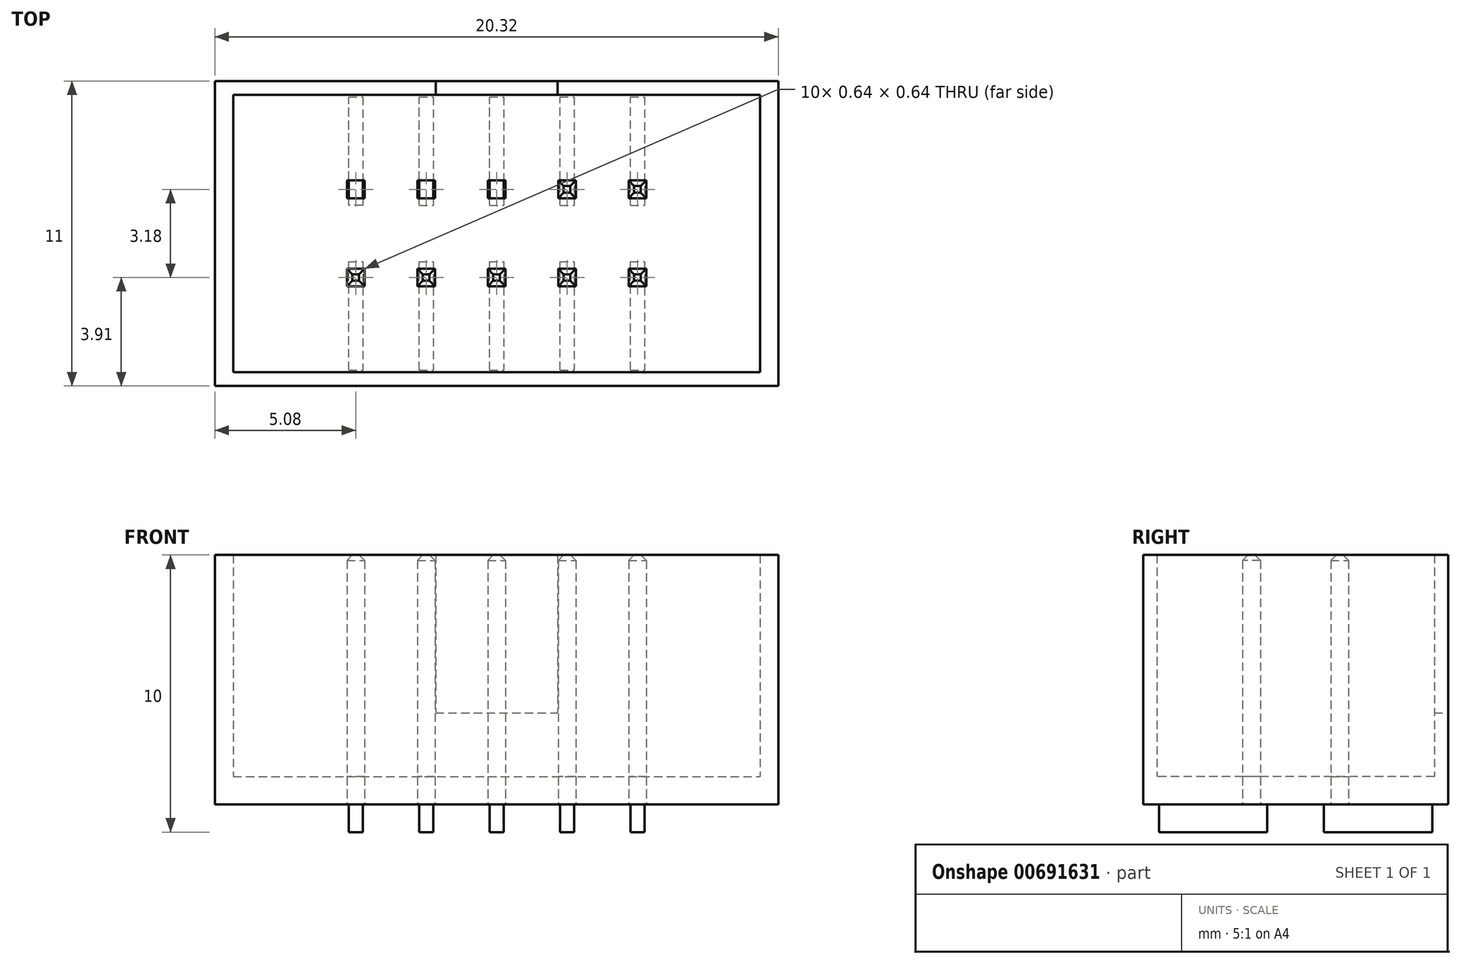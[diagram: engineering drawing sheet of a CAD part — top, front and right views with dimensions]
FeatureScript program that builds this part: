
annotation { "Feature Type Name" : "Feature", "Feature Type Description" : "" }
export const myFeature = defineFeature(function(context is Context, id is Id, definition is map)
    precondition{}
    {
        {
            var Q0;
            Q0=qCreatedBy(makeId("Top.planeOp"),FACE);
            var sketch = newSketch(context, id + "F0", { "sketchPlane" : qUnion([Q0])});
            skLineSegment(sketch, "E0.bottom", {"start": v(10.16, 5.5) * mm, "end": v(-10.16, 5.5) * mm});
            skLineSegment(sketch, "E0.top", {"start": v(10.16, -5.5) * mm, "end": v(-10.16, -5.5) * mm});
            skLineSegment(sketch, "E0.left", {"start": v(10.16, 5.5) * mm, "end": v(10.16, -5.5) * mm});
            skLineSegment(sketch, "E0.right", {"start": v(-10.16, 5.5) * mm, "end": v(-10.16, -5.5) * mm});
            skPoint(sketch, "E0.middle", {"position": v(0, 0) * mm});
            skLineSegment(sketch, "E1.bottom", {"start": v(-9.5, 5) * mm, "end": v(9.5, 5) * mm});
            skLineSegment(sketch, "E1.top", {"start": v(-9.5, -5) * mm, "end": v(9.5, -5) * mm});
            skLineSegment(sketch, "E1.left", {"start": v(-9.5, 5) * mm, "end": v(-9.5, -5) * mm});
            skLineSegment(sketch, "E1.right", {"start": v(9.5, 5) * mm, "end": v(9.5, -5) * mm});
            skLineSegment(sketch, "E2", {"start": v(-0.32, 1.27) * mm, "end": v(0.32, 1.27) * mm});
            skLineSegment(sketch, "E3", {"start": v(-0.32, 1.27) * mm, "end": v(-0.32, 1.9) * mm});
            skLineSegment(sketch, "E4", {"start": v(-0.32, 1.9) * mm, "end": v(0.32, 1.9) * mm});
            skLineSegment(sketch, "E5", {"start": v(0.32, 1.9) * mm, "end": v(0.32, 1.27) * mm});
            skLineSegment(sketch, "E6.MirrorCS", {"start": v(0.32, 1.27) * mm, "end": v(-0.32, 1.27) * mm});
            skLineSegment(sketch, "E7.MirrorCS", {"start": v(-0.32, 1.9) * mm, "end": v(-0.32, 1.27) * mm});
            skLineSegment(sketch, "E8.MirrorCS", {"start": v(0.32, 1.9) * mm, "end": v(-0.32, 1.9) * mm});
            skLineSegment(sketch, "E9.MirrorCS", {"start": v(0.32, 1.27) * mm, "end": v(0.32, 1.9) * mm});
            skLineSegment(sketch, "E10.MirrorCS", {"start": v(0.32, -1.27) * mm, "end": v(-0.32, -1.27) * mm});
            skLineSegment(sketch, "E11.MirrorCS", {"start": v(-0.32, -1.27) * mm, "end": v(-0.32, -1.9) * mm});
            skLineSegment(sketch, "E12.MirrorCS", {"start": v(0.32, -1.9) * mm, "end": v(-0.32, -1.9) * mm});
            skLineSegment(sketch, "E13.MirrorCS", {"start": v(0.32, -1.27) * mm, "end": v(0.32, -1.9) * mm});
            skLineSegment(sketch, "E14.1.0.0", {"start": v(2.22, 1.9) * mm, "end": v(2.86, 1.9) * mm});
            skLineSegment(sketch, "E14.1.0.1", {"start": v(2.22, 1.27) * mm, "end": v(2.22, 1.91) * mm});
            skLineSegment(sketch, "E14.1.0.2", {"start": v(2.22, 1.27) * mm, "end": v(2.86, 1.27) * mm});
            skLineSegment(sketch, "E14.1.0.3", {"start": v(2.86, 1.27) * mm, "end": v(2.86, 1.91) * mm});
            skLineSegment(sketch, "E14.1.0.4", {"start": v(2.22, -1.27) * mm, "end": v(2.22, -1.9) * mm});
            skLineSegment(sketch, "E14.1.0.5", {"start": v(2.86, -1.27) * mm, "end": v(2.22, -1.27) * mm});
            skLineSegment(sketch, "E14.1.0.6", {"start": v(2.86, -1.27) * mm, "end": v(2.86, -1.9) * mm});
            skLineSegment(sketch, "E14.1.0.7", {"start": v(2.86, -1.9) * mm, "end": v(2.22, -1.9) * mm});
            skLineSegment(sketch, "E14.2.0.0", {"start": v(4.76, 1.9) * mm, "end": v(5.4, 1.9) * mm});
            skLineSegment(sketch, "E14.2.0.1", {"start": v(4.76, 1.27) * mm, "end": v(4.76, 1.91) * mm});
            skLineSegment(sketch, "E14.2.0.2", {"start": v(4.76, 1.27) * mm, "end": v(5.4, 1.27) * mm});
            skLineSegment(sketch, "E14.2.0.3", {"start": v(5.4, 1.27) * mm, "end": v(5.4, 1.91) * mm});
            skLineSegment(sketch, "E14.2.0.4", {"start": v(4.76, -1.27) * mm, "end": v(4.76, -1.9) * mm});
            skLineSegment(sketch, "E14.2.0.5", {"start": v(5.4, -1.27) * mm, "end": v(4.76, -1.27) * mm});
            skLineSegment(sketch, "E14.2.0.6", {"start": v(5.4, -1.27) * mm, "end": v(5.4, -1.9) * mm});
            skLineSegment(sketch, "E14.2.0.7", {"start": v(5.4, -1.9) * mm, "end": v(4.76, -1.9) * mm});
            skLineSegment(sketch, "E14.direction1", {"start": v(-0.32, -1.9) * mm, "end": v(2.22, -1.9) * mm, "construction": true});
            skLineSegment(sketch, "E15.1.0.0", {"start": v(-2.22, -1.27) * mm, "end": v(-2.86, -1.27) * mm});
            skLineSegment(sketch, "E15.1.0.1", {"start": v(-2.22, -1.9) * mm, "end": v(-2.86, -1.9) * mm});
            skLineSegment(sketch, "E15.1.0.2", {"start": v(-2.22, 1.27) * mm, "end": v(-2.22, 1.9) * mm});
            skLineSegment(sketch, "E15.1.0.3", {"start": v(-2.86, -1.27) * mm, "end": v(-2.86, -1.9) * mm});
            skLineSegment(sketch, "E15.1.0.4", {"start": v(-2.86, 1.27) * mm, "end": v(-2.86, 1.9) * mm});
            skPoint(sketch, "E15.1.0.5", {"position": v(-2.54, 0) * mm});
            skLineSegment(sketch, "E15.1.0.6", {"start": v(-2.86, 1.27) * mm, "end": v(-2.22, 1.27) * mm});
            skLineSegment(sketch, "E15.1.0.7", {"start": v(-2.22, -1.27) * mm, "end": v(-2.22, -1.9) * mm});
            skLineSegment(sketch, "E15.1.0.8", {"start": v(-2.22, 1.9) * mm, "end": v(-2.86, 1.9) * mm});
            skPoint(sketch, "E15.1.0.9", {"position": v(-2.54, 0) * mm});
            skLineSegment(sketch, "E15.1.0.10", {"start": v(-2.86, 1.9) * mm, "end": v(-2.22, 1.9) * mm});
            skLineSegment(sketch, "E15.1.0.11", {"start": v(-2.22, 1.27) * mm, "end": v(-2.86, 1.27) * mm});
            skLineSegment(sketch, "E15.1.0.12", {"start": v(-2.86, 1.27) * mm, "end": v(-2.86, 1.9) * mm});
            skLineSegment(sketch, "E15.1.0.13", {"start": v(-2.22, 1.9) * mm, "end": v(-2.22, 1.27) * mm});
            skLineSegment(sketch, "E15.1.0.14", {"start": v(-2.86, 1.27) * mm, "end": v(-2.22, 1.27) * mm});
            skLineSegment(sketch, "E15.1.0.15", {"start": v(-2.22, 1.9) * mm, "end": v(-2.86, 1.9) * mm});
            skLineSegment(sketch, "E15.1.0.16", {"start": v(-2.86, 1.9) * mm, "end": v(-2.86, 1.27) * mm});
            skLineSegment(sketch, "E15.1.0.17", {"start": v(-2.22, 1.27) * mm, "end": v(-2.22, 1.9) * mm});
            skLineSegment(sketch, "E15.1.0.18", {"start": v(-2.22, 1.27) * mm, "end": v(-2.86, 1.27) * mm});
            skLineSegment(sketch, "E15.2.0.0", {"start": v(-4.76, -1.27) * mm, "end": v(-5.4, -1.27) * mm});
            skLineSegment(sketch, "E15.2.0.1", {"start": v(-4.76, -1.9) * mm, "end": v(-5.4, -1.9) * mm});
            skLineSegment(sketch, "E15.2.0.2", {"start": v(-4.76, 1.27) * mm, "end": v(-4.76, 1.9) * mm});
            skLineSegment(sketch, "E15.2.0.3", {"start": v(-5.4, -1.27) * mm, "end": v(-5.4, -1.9) * mm});
            skLineSegment(sketch, "E15.2.0.4", {"start": v(-5.4, 1.27) * mm, "end": v(-5.4, 1.9) * mm});
            skPoint(sketch, "E15.2.0.5", {"position": v(-5.08, 0) * mm});
            skLineSegment(sketch, "E15.2.0.6", {"start": v(-5.4, 1.27) * mm, "end": v(-4.76, 1.27) * mm});
            skLineSegment(sketch, "E15.2.0.7", {"start": v(-4.76, -1.27) * mm, "end": v(-4.76, -1.9) * mm});
            skLineSegment(sketch, "E15.2.0.8", {"start": v(-4.76, 1.9) * mm, "end": v(-5.4, 1.9) * mm});
            skPoint(sketch, "E15.2.0.9", {"position": v(-5.08, 0) * mm});
            skLineSegment(sketch, "E15.2.0.10", {"start": v(-5.4, 1.9) * mm, "end": v(-4.76, 1.9) * mm});
            skLineSegment(sketch, "E15.2.0.11", {"start": v(-4.76, 1.27) * mm, "end": v(-5.4, 1.27) * mm});
            skLineSegment(sketch, "E15.2.0.12", {"start": v(-5.4, 1.27) * mm, "end": v(-5.4, 1.9) * mm});
            skLineSegment(sketch, "E15.2.0.13", {"start": v(-4.76, 1.9) * mm, "end": v(-4.76, 1.27) * mm});
            skLineSegment(sketch, "E15.2.0.14", {"start": v(-5.4, 1.27) * mm, "end": v(-4.76, 1.27) * mm});
            skLineSegment(sketch, "E15.2.0.15", {"start": v(-4.76, 1.9) * mm, "end": v(-5.4, 1.9) * mm});
            skLineSegment(sketch, "E15.2.0.16", {"start": v(-5.4, 1.9) * mm, "end": v(-5.4, 1.27) * mm});
            skLineSegment(sketch, "E15.2.0.17", {"start": v(-4.76, 1.27) * mm, "end": v(-4.76, 1.9) * mm});
            skLineSegment(sketch, "E15.2.0.18", {"start": v(-4.76, 1.27) * mm, "end": v(-5.4, 1.27) * mm});
            skLineSegment(sketch, "E15.direction1", {"start": v(-0.32, -1.9) * mm, "end": v(-2.86, -1.9) * mm, "construction": true});
            skSolve(sketch);
        }
        {
            var Q0;
            Q0=makeQuery(id+"F0.imprint","IMPRINT",FACE,{"disambiguationData":[TD([[makeQuery(id+"F0.imprint","IMPRINT",EDGE,{"derivedFrom":sQuery(id+"F0.wireOp",EDGE,"E0.bottom")}),1.0]])]});
            extrude(context, id + "F1", {"entities" : qUnion([Q0]), "depth" : 9 * mm, "offsetDistance" : 25 * mm});
        }
        {
            var Q0;
            Q0=makeQuery(id+"F0.imprint","IMPRINT",FACE,{"disambiguationData":[TD([[makeQuery(id+"F0.imprint","IMPRINT",EDGE,{"derivedFrom":sQuery(id+"F0.wireOp",EDGE,"E1.bottom")}),-1.0]])]});
            extrude(context, id + "F2", {"entities" : qUnion([Q0]), "operationType" : NewBodyOperationType.ADD, "depth" : 1 * mm, "offsetDistance" : 25 * mm});
        }
        {
            var Q0;
            Q0=makeQuery(id+"F0.imprint","IMPRINT",FACE,{"disambiguationData":[TD([[makeQuery(id+"F0.imprint","IMPRINT",EDGE,{"derivedFrom":sQuery(id+"F0.wireOp",EDGE,"2ed2c639-f61c-45ec-8934-820072ae5572.2.0.0")}),1.0]])]});
            var Q1;
            Q1=makeQuery(id+"F0.imprint","IMPRINT",FACE,{"disambiguationData":[TD([[makeQuery(id+"F0.imprint","IMPRINT",EDGE,{"derivedFrom":sQuery(id+"F0.wireOp",EDGE,"2ed2c639-f61c-45ec-8934-820072ae5572.2.0.4")}),1.0]])]});
            var Q2;
            Q2=makeQuery(id+"F0.imprint","IMPRINT",FACE,{"disambiguationData":[TD([[makeQuery(id+"F0.imprint","IMPRINT",EDGE,{"derivedFrom":sQuery(id+"F0.wireOp",EDGE,"2ed2c639-f61c-45ec-8934-820072ae5572.1.0.0")}),1.0]])]});
            var Q3;
            Q3=makeQuery(id+"F0.imprint","IMPRINT",FACE,{"disambiguationData":[TD([[makeQuery(id+"F0.imprint","IMPRINT",EDGE,{"derivedFrom":sQuery(id+"F0.wireOp",EDGE,"2ed2c639-f61c-45ec-8934-820072ae5572.1.0.4")}),1.0]])]});
            var Q4;
            Q4=makeQuery(id+"F0.imprint","IMPRINT",FACE,{"disambiguationData":[TD([[makeQuery(id+"F0.imprint","IMPRINT",EDGE,{"derivedFrom":sQuery(id+"F0.wireOp",EDGE,"E10.MirrorCS")}),1.0]])]});
            var Q5;
            Q5=makeQuery(id+"F0.imprint","IMPRINT",FACE,{"disambiguationData":[TD([[makeQuery(id+"F0.imprint","IMPRINT",EDGE,{"derivedFrom":sQuery(id+"F0.wireOp",EDGE,"E9.MirrorCS")}),1.0]])]});
            var Q6;
            Q6=makeQuery(id+"F0.imprint","IMPRINT",FACE,{"disambiguationData":[TD([[makeQuery(id+"F0.imprint","IMPRINT",EDGE,{"derivedFrom":sQuery(id+"F0.wireOp",EDGE,"E14.1.0.0")}),-1.0]])]});
            var Q7;
            Q7=makeQuery(id+"F0.imprint","IMPRINT",FACE,{"disambiguationData":[TD([[makeQuery(id+"F0.imprint","IMPRINT",EDGE,{"derivedFrom":sQuery(id+"F0.wireOp",EDGE,"E14.1.0.4")}),1.0]])]});
            var Q8;
            Q8=makeQuery(id+"F0.imprint","IMPRINT",FACE,{"disambiguationData":[TD([[makeQuery(id+"F0.imprint","IMPRINT",EDGE,{"derivedFrom":sQuery(id+"F0.wireOp",EDGE,"E14.2.0.0")}),-1.0]])]});
            var Q9;
            Q9=makeQuery(id+"F0.imprint","IMPRINT",FACE,{"disambiguationData":[TD([[makeQuery(id+"F0.imprint","IMPRINT",EDGE,{"derivedFrom":sQuery(id+"F0.wireOp",EDGE,"E14.2.0.4")}),1.0]])]});
            extrude(context, id + "F3", {"entities" : qUnion([Q0, Q1, Q2, Q3, Q4, Q5, Q6, Q7, Q8, Q9]), "depth" : 9 * mm, "offsetDistance" : 25 * mm});
        }
        {
            var Q0;
            Q0=makeQuery(id+"F3.opExtrude","CAP_EDGE",EDGE,{"disambiguationData":[OSD([sQuery(id+"F0.wireOp",EDGE,"2ed2c639-f61c-45ec-8934-820072ae5572.2.0.2")])],"isStart":false});
            var Q1;
            Q1=makeQuery(id+"F3.opExtrude","CAP_EDGE",EDGE,{"disambiguationData":[OSD([sQuery(id+"F0.wireOp",EDGE,"2ed2c639-f61c-45ec-8934-820072ae5572.2.0.3")])],"isStart":false});
            var Q2;
            Q2=makeQuery(id+"F3.opExtrude","CAP_EDGE",EDGE,{"disambiguationData":[OSD([sQuery(id+"F0.wireOp",EDGE,"2ed2c639-f61c-45ec-8934-820072ae5572.2.0.0")])],"isStart":false});
            var Q3;
            Q3=makeQuery(id+"F3.opExtrude","CAP_EDGE",EDGE,{"disambiguationData":[OSD([sQuery(id+"F0.wireOp",EDGE,"2ed2c639-f61c-45ec-8934-820072ae5572.2.0.1")])],"isStart":false});
            var Q4;
            Q4=makeQuery(id+"F3.opExtrude","CAP_EDGE",EDGE,{"disambiguationData":[OSD([sQuery(id+"F0.wireOp",EDGE,"2ed2c639-f61c-45ec-8934-820072ae5572.2.0.4")])],"isStart":false});
            var Q5;
            Q5=makeQuery(id+"F3.opExtrude","CAP_EDGE",EDGE,{"disambiguationData":[OSD([sQuery(id+"F0.wireOp",EDGE,"2ed2c639-f61c-45ec-8934-820072ae5572.2.0.6")])],"isStart":false});
            var Q6;
            Q6=makeQuery(id+"F3.opExtrude","CAP_EDGE",EDGE,{"disambiguationData":[OSD([sQuery(id+"F0.wireOp",EDGE,"2ed2c639-f61c-45ec-8934-820072ae5572.2.0.7")])],"isStart":false});
            var Q7;
            Q7=makeQuery(id+"F3.opExtrude","CAP_EDGE",EDGE,{"disambiguationData":[OSD([sQuery(id+"F0.wireOp",EDGE,"2ed2c639-f61c-45ec-8934-820072ae5572.2.0.5")])],"isStart":false});
            var Q8;
            Q8=makeQuery(id+"F3.opExtrude","CAP_EDGE",EDGE,{"disambiguationData":[OSD([sQuery(id+"F0.wireOp",EDGE,"2ed2c639-f61c-45ec-8934-820072ae5572.1.0.3")])],"isStart":false});
            var Q9;
            Q9=makeQuery(id+"F3.opExtrude","CAP_EDGE",EDGE,{"disambiguationData":[OSD([sQuery(id+"F0.wireOp",EDGE,"2ed2c639-f61c-45ec-8934-820072ae5572.1.0.1")])],"isStart":false});
            var Q10;
            Q10=makeQuery(id+"F3.opExtrude","CAP_EDGE",EDGE,{"disambiguationData":[OSD([sQuery(id+"F0.wireOp",EDGE,"2ed2c639-f61c-45ec-8934-820072ae5572.1.0.2")])],"isStart":false});
            var Q11;
            Q11=makeQuery(id+"F3.opExtrude","CAP_EDGE",EDGE,{"disambiguationData":[OSD([sQuery(id+"F0.wireOp",EDGE,"2ed2c639-f61c-45ec-8934-820072ae5572.1.0.0")])],"isStart":false});
            var Q12;
            Q12=makeQuery(id+"F3.opExtrude","CAP_EDGE",EDGE,{"disambiguationData":[OSD([sQuery(id+"F0.wireOp",EDGE,"2ed2c639-f61c-45ec-8934-820072ae5572.1.0.6")])],"isStart":false});
            var Q13;
            Q13=makeQuery(id+"F3.opExtrude","CAP_EDGE",EDGE,{"disambiguationData":[OSD([sQuery(id+"F0.wireOp",EDGE,"2ed2c639-f61c-45ec-8934-820072ae5572.1.0.7")])],"isStart":false});
            var Q14;
            Q14=makeQuery(id+"F3.opExtrude","CAP_EDGE",EDGE,{"disambiguationData":[OSD([sQuery(id+"F0.wireOp",EDGE,"2ed2c639-f61c-45ec-8934-820072ae5572.1.0.5")])],"isStart":false});
            var Q15;
            Q15=makeQuery(id+"F3.opExtrude","CAP_EDGE",EDGE,{"disambiguationData":[OSD([sQuery(id+"F0.wireOp",EDGE,"2ed2c639-f61c-45ec-8934-820072ae5572.1.0.4")])],"isStart":false});
            var Q16;
            Q16=makeQuery(id+"F3.opExtrude","CAP_EDGE",EDGE,{"disambiguationData":[OSD([sQuery(id+"F0.wireOp",EDGE,"E3")])],"isStart":false});
            var Q17;
            Q17=makeQuery(id+"F3.opExtrude","CAP_EDGE",EDGE,{"disambiguationData":[OSD([sQuery(id+"F0.wireOp",EDGE,"E2")])],"isStart":false});
            var Q18;
            Q18=makeQuery(id+"F3.opExtrude","CAP_EDGE",EDGE,{"disambiguationData":[OSD([sQuery(id+"F0.wireOp",EDGE,"E9.MirrorCS")])],"isStart":false});
            var Q19;
            Q19=makeQuery(id+"F3.opExtrude","CAP_EDGE",EDGE,{"disambiguationData":[OSD([sQuery(id+"F0.wireOp",EDGE,"E8.MirrorCS")])],"isStart":false});
            var Q20;
            Q20=makeQuery(id+"F3.opExtrude","CAP_EDGE",EDGE,{"disambiguationData":[OSD([sQuery(id+"F0.wireOp",EDGE,"E10.MirrorCS")])],"isStart":false});
            var Q21;
            Q21=makeQuery(id+"F3.opExtrude","CAP_EDGE",EDGE,{"disambiguationData":[OSD([sQuery(id+"F0.wireOp",EDGE,"E11.MirrorCS")])],"isStart":false});
            var Q22;
            Q22=makeQuery(id+"F3.opExtrude","CAP_EDGE",EDGE,{"disambiguationData":[OSD([sQuery(id+"F0.wireOp",EDGE,"E12.MirrorCS")])],"isStart":false});
            var Q23;
            Q23=makeQuery(id+"F3.opExtrude","CAP_EDGE",EDGE,{"disambiguationData":[OSD([sQuery(id+"F0.wireOp",EDGE,"E13.MirrorCS")])],"isStart":false});
            var Q24;
            Q24=makeQuery(id+"F3.opExtrude","CAP_EDGE",EDGE,{"disambiguationData":[OSD([sQuery(id+"F0.wireOp",EDGE,"E14.1.0.4")])],"isStart":false});
            var Q25;
            Q25=makeQuery(id+"F3.opExtrude","CAP_EDGE",EDGE,{"disambiguationData":[OSD([sQuery(id+"F0.wireOp",EDGE,"E14.1.0.7")])],"isStart":false});
            var Q26;
            Q26=makeQuery(id+"F3.opExtrude","CAP_EDGE",EDGE,{"disambiguationData":[OSD([sQuery(id+"F0.wireOp",EDGE,"E14.1.0.6")])],"isStart":false});
            var Q27;
            Q27=makeQuery(id+"F3.opExtrude","CAP_EDGE",EDGE,{"disambiguationData":[OSD([sQuery(id+"F0.wireOp",EDGE,"E14.1.0.5")])],"isStart":false});
            var Q28;
            Q28=makeQuery(id+"F3.opExtrude","CAP_EDGE",EDGE,{"disambiguationData":[OSD([sQuery(id+"F0.wireOp",EDGE,"E14.1.0.1")])],"isStart":false});
            var Q29;
            Q29=makeQuery(id+"F3.opExtrude","CAP_EDGE",EDGE,{"disambiguationData":[OSD([sQuery(id+"F0.wireOp",EDGE,"E14.1.0.2")])],"isStart":false});
            var Q30;
            Q30=makeQuery(id+"F3.opExtrude","CAP_EDGE",EDGE,{"disambiguationData":[OSD([sQuery(id+"F0.wireOp",EDGE,"E14.1.0.3")])],"isStart":false});
            var Q31;
            Q31=makeQuery(id+"F3.opExtrude","CAP_EDGE",EDGE,{"disambiguationData":[OSD([sQuery(id+"F0.wireOp",EDGE,"E14.1.0.0")])],"isStart":false});
            var Q32;
            Q32=makeQuery(id+"F3.opExtrude","CAP_EDGE",EDGE,{"disambiguationData":[OSD([sQuery(id+"F0.wireOp",EDGE,"E14.2.0.1")])],"isStart":false});
            var Q33;
            Q33=makeQuery(id+"F3.opExtrude","CAP_EDGE",EDGE,{"disambiguationData":[OSD([sQuery(id+"F0.wireOp",EDGE,"E14.2.0.2")])],"isStart":false});
            var Q34;
            Q34=makeQuery(id+"F3.opExtrude","CAP_EDGE",EDGE,{"disambiguationData":[OSD([sQuery(id+"F0.wireOp",EDGE,"E14.2.0.0")])],"isStart":false});
            var Q35;
            Q35=makeQuery(id+"F3.opExtrude","CAP_EDGE",EDGE,{"disambiguationData":[OSD([sQuery(id+"F0.wireOp",EDGE,"E14.2.0.3")])],"isStart":false});
            var Q36;
            Q36=makeQuery(id+"F3.opExtrude","CAP_EDGE",EDGE,{"disambiguationData":[OSD([sQuery(id+"F0.wireOp",EDGE,"E14.2.0.5")])],"isStart":false});
            var Q37;
            Q37=makeQuery(id+"F3.opExtrude","CAP_EDGE",EDGE,{"disambiguationData":[OSD([sQuery(id+"F0.wireOp",EDGE,"E14.2.0.4")])],"isStart":false});
            var Q38;
            Q38=makeQuery(id+"F3.opExtrude","CAP_EDGE",EDGE,{"disambiguationData":[OSD([sQuery(id+"F0.wireOp",EDGE,"E14.2.0.7")])],"isStart":false});
            var Q39;
            Q39=makeQuery(id+"F3.opExtrude","CAP_EDGE",EDGE,{"disambiguationData":[OSD([sQuery(id+"F0.wireOp",EDGE,"E14.2.0.6")])],"isStart":false});
            chamfer(context, id + "F4", {"entities" : qUnion([Q0, Q1, Q2, Q3, Q4, Q5, Q6, Q7, Q8, Q9, Q10, Q11, Q12, Q13, Q14, Q15, Q16, Q17, Q18, Q19, Q20, Q21, Q22, Q23, Q24, Q25, Q26, Q27, Q28, Q29, Q30, Q31, Q32, Q33, Q34, Q35, Q36, Q37, Q38, Q39]), "width" : 0.2 * mm, "tangentPropagation" : true});
        }
        {
            var Q0;
            Q0=qCreatedBy(makeId("Top.planeOp"),FACE);
            cPlane(context, id + "F5", {"entities" : qUnion([Q0]), "cplaneType" : CPlaneType.OFFSET, "offset" : 3.3 * mm, "width" : 150 * mm, "height" : 150 * mm});
        }
        {
            var Q0;
            Q0=qCreatedBy(id+"F5.planeOp",FACE);
            var sketch = newSketch(context, id + "F6", { "sketchPlane" : qUnion([Q0])});
            skLineSegment(sketch, "E16", {"start": v(-2.2, 5) * mm, "end": v(2.2, 5) * mm});
            skLineSegment(sketch, "E17", {"start": v(-2.2, 5) * mm, "end": v(-2.2, 5.5) * mm});
            skLineSegment(sketch, "E18", {"start": v(-2.2, 5.5) * mm, "end": v(2.2, 5.5) * mm});
            skLineSegment(sketch, "E19", {"start": v(2.2, 5.5) * mm, "end": v(2.2, 5) * mm});
            skSolve(sketch);
        }
        {
            var Q0;
            Q0=makeQuery(id+"F6.imprint","IMPRINT",FACE,{"disambiguationData":[TD([[makeQuery(id+"F6.imprint","IMPRINT",EDGE,{"derivedFrom":sQuery(id+"F6.wireOp",EDGE,"E16")}),1.0]])]});
            extrude(context, id + "F7", {"entities" : qUnion([Q0]), "operationType" : NewBodyOperationType.REMOVE, "depth" : 5.7 * mm, "offsetDistance" : 25 * mm});
        }
        {
            var Q0;
            Q0=qCreatedBy(makeId("Top.planeOp"),FACE);
            cPlane(context, id + "F8", {"entities" : qUnion([Q0]), "cplaneType" : CPlaneType.OFFSET, "offset" : 1 * mm, "oppositeDirection" : true, "width" : 150 * mm, "height" : 150 * mm});
        }
        {
            var Q0;
            Q0=qCreatedBy(id+"F8.planeOp",FACE);
            var sketch = newSketch(context, id + "F9", { "sketchPlane" : qUnion([Q0])});
            skLineSegment(sketch, "E20", {"start": v(-5.34, 1.02) * mm, "end": v(-5.34, 4.93) * mm});
            skLineSegment(sketch, "E21", {"start": v(-5.34, 4.93) * mm, "end": v(-4.83, 4.93) * mm});
            skLineSegment(sketch, "E22", {"start": v(-4.83, 4.93) * mm, "end": v(-4.83, 1.02) * mm});
            skLineSegment(sketch, "E23", {"start": v(-4.83, 1.02) * mm, "end": v(-5.34, 1.02) * mm});
            skLineSegment(sketch, "E24.0.1.0", {"start": v(-5.34, -4.93) * mm, "end": v(-5.34, -1.02) * mm});
            skLineSegment(sketch, "E24.0.1.1", {"start": v(-5.34, -1.02) * mm, "end": v(-4.83, -1.02) * mm});
            skLineSegment(sketch, "E24.0.1.2", {"start": v(-4.83, -1.02) * mm, "end": v(-4.83, -4.93) * mm});
            skLineSegment(sketch, "E24.1.0.0", {"start": v(-2.8, 1.02) * mm, "end": v(-2.8, 4.93) * mm});
            skLineSegment(sketch, "E24.1.0.1", {"start": v(-2.8, 4.93) * mm, "end": v(-2.29, 4.93) * mm});
            skLineSegment(sketch, "E24.1.0.2", {"start": v(-2.29, 4.93) * mm, "end": v(-2.29, 1.02) * mm});
            skLineSegment(sketch, "E24.1.1.0", {"start": v(-2.8, -4.93) * mm, "end": v(-2.8, -1.02) * mm});
            skLineSegment(sketch, "E24.1.1.1", {"start": v(-2.8, -1.02) * mm, "end": v(-2.29, -1.02) * mm});
            skLineSegment(sketch, "E24.1.1.2", {"start": v(-2.29, -1.02) * mm, "end": v(-2.29, -4.93) * mm});
            skLineSegment(sketch, "E24.2.0.0", {"start": v(-0.26, 1.02) * mm, "end": v(-0.26, 4.93) * mm});
            skLineSegment(sketch, "E24.2.0.1", {"start": v(-0.26, 4.93) * mm, "end": v(0.25, 4.93) * mm});
            skLineSegment(sketch, "E24.2.0.2", {"start": v(0.25, 4.93) * mm, "end": v(0.25, 1.02) * mm});
            skLineSegment(sketch, "E24.2.1.0", {"start": v(-0.26, -4.93) * mm, "end": v(-0.26, -1.02) * mm});
            skLineSegment(sketch, "E24.2.1.1", {"start": v(-0.26, -1.02) * mm, "end": v(0.25, -1.02) * mm});
            skLineSegment(sketch, "E24.2.1.2", {"start": v(0.25, -1.02) * mm, "end": v(0.25, -4.93) * mm});
            skLineSegment(sketch, "E24.3.0.0", {"start": v(2.28, 1.02) * mm, "end": v(2.28, 4.93) * mm});
            skLineSegment(sketch, "E24.3.0.1", {"start": v(2.28, 4.93) * mm, "end": v(2.8, 4.93) * mm});
            skLineSegment(sketch, "E24.3.0.2", {"start": v(2.8, 4.93) * mm, "end": v(2.8, 1.02) * mm});
            skLineSegment(sketch, "E24.3.1.0", {"start": v(2.28, -4.93) * mm, "end": v(2.28, -1.02) * mm});
            skLineSegment(sketch, "E24.3.1.1", {"start": v(2.28, -1.02) * mm, "end": v(2.8, -1.02) * mm});
            skLineSegment(sketch, "E24.3.1.2", {"start": v(2.8, -1.02) * mm, "end": v(2.8, -4.93) * mm});
            skLineSegment(sketch, "E24.4.0.0", {"start": v(4.82, 1.02) * mm, "end": v(4.82, 4.93) * mm});
            skLineSegment(sketch, "E24.4.0.1", {"start": v(4.82, 4.93) * mm, "end": v(5.33, 4.93) * mm});
            skLineSegment(sketch, "E24.4.0.2", {"start": v(5.33, 4.93) * mm, "end": v(5.33, 1.02) * mm});
            skLineSegment(sketch, "E24.4.1.0", {"start": v(4.82, -4.93) * mm, "end": v(4.82, -1.02) * mm});
            skLineSegment(sketch, "E24.4.1.1", {"start": v(4.82, -1.02) * mm, "end": v(5.33, -1.02) * mm});
            skLineSegment(sketch, "E24.4.1.2", {"start": v(5.33, -1.02) * mm, "end": v(5.33, -4.93) * mm});
            skLineSegment(sketch, "E24.direction1", {"start": v(-5.34, 1.02) * mm, "end": v(-2.8, 1.02) * mm, "construction": true});
            skLineSegment(sketch, "E24.direction2", {"start": v(-5.34, 1.02) * mm, "end": v(-5.34, -4.93) * mm, "construction": true});
            skLineSegment(sketch, "E25", {"start": v(-2.8, 1.02) * mm, "end": v(-2.29, 1.02) * mm});
            skLineSegment(sketch, "E26", {"start": v(-0.26, 1.02) * mm, "end": v(0.25, 1.02) * mm});
            skLineSegment(sketch, "E27", {"start": v(2.28, 1.02) * mm, "end": v(2.8, 1.02) * mm});
            skLineSegment(sketch, "E28", {"start": v(4.82, 1.02) * mm, "end": v(5.33, 1.02) * mm});
            skLineSegment(sketch, "E29", {"start": v(4.82, -4.93) * mm, "end": v(5.33, -4.93) * mm});
            skLineSegment(sketch, "E30", {"start": v(2.28, -4.93) * mm, "end": v(2.8, -4.93) * mm});
            skLineSegment(sketch, "E31", {"start": v(-0.26, -4.93) * mm, "end": v(0.25, -4.93) * mm});
            skLineSegment(sketch, "E32", {"start": v(-2.8, -4.93) * mm, "end": v(-2.29, -4.93) * mm});
            skLineSegment(sketch, "E33", {"start": v(-5.34, -4.93) * mm, "end": v(-4.83, -4.93) * mm});
            skSolve(sketch);
        }
        {
            var Q0;
            Q0=makeQuery(id+"F9.imprint","IMPRINT",FACE,{"disambiguationData":[TD([[makeQuery(id+"F9.imprint","IMPRINT",EDGE,{"derivedFrom":sQuery(id+"F9.wireOp",EDGE,"E24.4.1.0")}),-1.0]])]});
            var Q1;
            Q1=makeQuery(id+"F9.imprint","IMPRINT",FACE,{"disambiguationData":[TD([[makeQuery(id+"F9.imprint","IMPRINT",EDGE,{"derivedFrom":sQuery(id+"F9.wireOp",EDGE,"E24.3.1.0")}),-1.0]])]});
            var Q2;
            Q2=makeQuery(id+"F9.imprint","IMPRINT",FACE,{"disambiguationData":[TD([[makeQuery(id+"F9.imprint","IMPRINT",EDGE,{"derivedFrom":sQuery(id+"F9.wireOp",EDGE,"E24.2.1.0")}),-1.0]])]});
            var Q3;
            Q3=makeQuery(id+"F9.imprint","IMPRINT",FACE,{"disambiguationData":[TD([[makeQuery(id+"F9.imprint","IMPRINT",EDGE,{"derivedFrom":sQuery(id+"F9.wireOp",EDGE,"E24.1.1.0")}),-1.0]])]});
            var Q4;
            Q4=makeQuery(id+"F9.imprint","IMPRINT",FACE,{"disambiguationData":[TD([[makeQuery(id+"F9.imprint","IMPRINT",EDGE,{"derivedFrom":sQuery(id+"F9.wireOp",EDGE,"E24.0.1.0")}),-1.0]])]});
            var Q5;
            Q5=makeQuery(id+"F9.imprint","IMPRINT",FACE,{"disambiguationData":[TD([[makeQuery(id+"F9.imprint","IMPRINT",EDGE,{"derivedFrom":sQuery(id+"F9.wireOp",EDGE,"E20")}),-1.0]])]});
            var Q6;
            Q6=makeQuery(id+"F9.imprint","IMPRINT",FACE,{"disambiguationData":[TD([[makeQuery(id+"F9.imprint","IMPRINT",EDGE,{"derivedFrom":sQuery(id+"F9.wireOp",EDGE,"E24.1.0.0")}),-1.0]])]});
            var Q7;
            Q7=makeQuery(id+"F9.imprint","IMPRINT",FACE,{"disambiguationData":[TD([[makeQuery(id+"F9.imprint","IMPRINT",EDGE,{"derivedFrom":sQuery(id+"F9.wireOp",EDGE,"E24.2.0.0")}),-1.0]])]});
            var Q8;
            Q8=makeQuery(id+"F9.imprint","IMPRINT",FACE,{"disambiguationData":[TD([[makeQuery(id+"F9.imprint","IMPRINT",EDGE,{"derivedFrom":sQuery(id+"F9.wireOp",EDGE,"E24.3.0.0")}),-1.0]])]});
            var Q9;
            Q9=makeQuery(id+"F9.imprint","IMPRINT",FACE,{"disambiguationData":[TD([[makeQuery(id+"F9.imprint","IMPRINT",EDGE,{"derivedFrom":sQuery(id+"F9.wireOp",EDGE,"E24.4.0.0")}),-1.0]])]});
            extrude(context, id + "F10", {"entities" : qUnion([Q0, Q1, Q2, Q3, Q4, Q5, Q6, Q7, Q8, Q9]), "depth" : 1 * mm, "offsetDistance" : 25 * mm});
        }
        {
            var Q0;
            Q0=makeQuery(id+"F0.imprint","IMPRINT",FACE,{"disambiguationData":[TD([[makeQuery(id+"F0.imprint","IMPRINT",EDGE,{"derivedFrom":sQuery(id+"F0.wireOp",EDGE,"E15.2.0.15")}),1.0]])]});
            var Q1;
            Q1=makeQuery(id+"F0.imprint","IMPRINT",FACE,{"disambiguationData":[TD([[makeQuery(id+"F0.imprint","IMPRINT",EDGE,{"derivedFrom":sQuery(id+"F0.wireOp",EDGE,"E15.1.0.15")}),1.0]])]});
            var Q2;
            Q2=makeQuery(id+"F0.imprint","IMPRINT",FACE,{"disambiguationData":[TD([[makeQuery(id+"F0.imprint","IMPRINT",EDGE,{"derivedFrom":sQuery(id+"F0.wireOp",EDGE,"E15.1.0.0")}),1.0]])]});
            var Q3;
            Q3=makeQuery(id+"F0.imprint","IMPRINT",FACE,{"disambiguationData":[TD([[makeQuery(id+"F0.imprint","IMPRINT",EDGE,{"derivedFrom":sQuery(id+"F0.wireOp",EDGE,"E15.2.0.0")}),1.0]])]});
            extrude(context, id + "F11", {"entities" : qUnion([Q0, Q1, Q2, Q3]), "depth" : 9 * mm, "offsetDistance" : 25 * mm});
        }
        {
            var Q0;
            Q0=makeQuery(id+"F11.opExtrude","CAP_EDGE",EDGE,{"disambiguationData":[OSD([sQuery(id+"F0.wireOp",EDGE,"E15.2.0.16")])],"isStart":false});
            var Q1;
            Q1=makeQuery(id+"F11.opExtrude","CAP_EDGE",EDGE,{"disambiguationData":[OSD([sQuery(id+"F0.wireOp",EDGE,"E15.2.0.15")])],"isStart":false});
            var Q2;
            Q2=makeQuery(id+"F11.opExtrude","CAP_EDGE",EDGE,{"disambiguationData":[OSD([sQuery(id+"F0.wireOp",EDGE,"E15.2.0.18")])],"isStart":false});
            var Q3;
            Q3=makeQuery(id+"F11.opExtrude","CAP_EDGE",EDGE,{"disambiguationData":[OSD([sQuery(id+"F0.wireOp",EDGE,"E15.2.0.17")])],"isStart":false});
            var Q4;
            Q4=makeQuery(id+"F11.opExtrude","CAP_EDGE",EDGE,{"disambiguationData":[OSD([sQuery(id+"F0.wireOp",EDGE,"E15.1.0.16")])],"isStart":false});
            var Q5;
            Q5=makeQuery(id+"F11.opExtrude","CAP_EDGE",EDGE,{"disambiguationData":[OSD([sQuery(id+"F0.wireOp",EDGE,"E15.1.0.15")])],"isStart":false});
            var Q6;
            Q6=makeQuery(id+"F11.opExtrude","CAP_EDGE",EDGE,{"disambiguationData":[OSD([sQuery(id+"F0.wireOp",EDGE,"E15.1.0.17")])],"isStart":false});
            var Q7;
            Q7=makeQuery(id+"F11.opExtrude","CAP_EDGE",EDGE,{"disambiguationData":[OSD([sQuery(id+"F0.wireOp",EDGE,"E15.1.0.18")])],"isStart":false});
            var Q8;
            Q8=makeQuery(id+"F11.opExtrude","CAP_EDGE",EDGE,{"disambiguationData":[OSD([sQuery(id+"F0.wireOp",EDGE,"E15.2.0.3")])],"isStart":false});
            var Q9;
            Q9=makeQuery(id+"F11.opExtrude","CAP_EDGE",EDGE,{"disambiguationData":[OSD([sQuery(id+"F0.wireOp",EDGE,"E15.2.0.0")])],"isStart":false});
            var Q10;
            Q10=makeQuery(id+"F11.opExtrude","CAP_EDGE",EDGE,{"disambiguationData":[OSD([sQuery(id+"F0.wireOp",EDGE,"E15.2.0.7")])],"isStart":false});
            var Q11;
            Q11=makeQuery(id+"F11.opExtrude","CAP_EDGE",EDGE,{"disambiguationData":[OSD([sQuery(id+"F0.wireOp",EDGE,"E15.2.0.1")])],"isStart":false});
            var Q12;
            Q12=makeQuery(id+"F11.opExtrude","CAP_EDGE",EDGE,{"disambiguationData":[OSD([sQuery(id+"F0.wireOp",EDGE,"E15.1.0.3")])],"isStart":false});
            var Q13;
            Q13=makeQuery(id+"F11.opExtrude","CAP_EDGE",EDGE,{"disambiguationData":[OSD([sQuery(id+"F0.wireOp",EDGE,"E15.1.0.1")])],"isStart":false});
            var Q14;
            Q14=makeQuery(id+"F11.opExtrude","CAP_EDGE",EDGE,{"disambiguationData":[OSD([sQuery(id+"F0.wireOp",EDGE,"E15.1.0.7")])],"isStart":false});
            var Q15;
            Q15=makeQuery(id+"F11.opExtrude","CAP_EDGE",EDGE,{"disambiguationData":[OSD([sQuery(id+"F0.wireOp",EDGE,"E15.1.0.0")])],"isStart":false});
            chamfer(context, id + "F12", {"entities" : qUnion([Q0, Q1, Q2, Q3, Q4, Q5, Q6, Q7, Q8, Q9, Q10, Q11, Q12, Q13, Q14, Q15]), "width" : 0.2 * mm, "tangentPropagation" : true});
        }
    });
